# Revit family: PRD_FrankeWS_UrnlFlshPps_FlushingPipe_ZAQUA057_ZAQUA058_ZAQUA059_ZAQUA060
name_source: partatom
category: Specialty Equipment
revit_build: Autodesk Revit 2018 (Build: 20190510_1515(x64)
units: mm (PartAtom-declared; Revit-internal decimal feet)

## family parameters
Always vertical = Yes
Cut with Voids When Loaded = No
OmniClass Number = 23.45.05.14.99
OmniClass Title = Other Sanitary Washing Plumbing Fixtures
Part Type = Normal
Room Calculation Point = No
Round Connector Dimension = Use Diameter
Shared = No
Work Plane-Based = No

## types (4) — shared parameters
AssetType = Fixed
BodyMaterial = PRD_AR_ChromatedBrass_HighPolished
Category = Pr_40_20_93_80, Urinal flush pipes
Color = Chrome
Description = Flushing pipe for PROTRONIC urinal flush valve for surface installation, length 200 mm, polished chromium-plated brass.
DurationUnit = year
Finish = Polished chrome
IfcExportAs = IfcPipeFittingType
IfcExportType = USERDEFINED
Manufacturer = KWC Group AG
ManufacturerName = KWC Group AG
ManufacturerURL = www.kwc.com
Material = Brass
NBSDescription = Urinal flush pipes
NBSReference = 45-35-70/356
NominalHeight = 200 mm  [stored 0.656168 ft]
PressureClass = 0.0 Pa
PressureRange = 0.0 Pa
ProductInformation = https://pim.kwc.com
Status = New
TemperatureRange = 0 °C
TypeOfFlushingPipe = Urinal pipe
URL = www.kwc.com
Uniclass2015Code = Pr_40_20_93_80
Uniclass2015Title = Urinal flush pipes
Uniclass2015Version = Products v1.17
Version = 1
WarrantyDurationUnit = year
zero-valued in all types: FittingLossFactor, NominalDepth, NominalWidth

## per-type parameters (varying)
| type | BIMObjectName | Crank | Features | GrossWeight | ModelNumber | Name | NetWeight | ProductCode | WithCrank | ZAQUA057 | ZAQUA058 | ZAQUA059 | ZAQUA060 |
| ZAQUA057 | PRD_AR_UrinalFlushPipes_FlushingPipe_ZAQUA057 |  | Straight, length 200 mm | 0.08 kg | 2000101459 | Flushing pipe ZAQUA057 | 0.08 kg |  | No | Yes | No | No | No |
| ZAQUA058 | PRD_AR_UrinalFlushPipes_FlushingPipe_ZAQUA058 | 20.00 mm | With crank 20 mm, length 200 mm | 0.16 kg | 2000101460 | Flushing pipe ZAQUA058 | 0.09 kg | 209.0000.031 | Yes | No | Yes | No | No |
| ZAQUA059 | PRD_AR_UrinalFlushPipes_FlushingPipe_ZAQUA059 | 30.00 mm | With crank 30 mm, length 200 mm | 0.16 kg | 2000101461 | Flushing pipe ZAQUA059 | 0.09 kg | 209.0638.156 | Yes | No | No | Yes | No |
| ZAQUA060 | PRD_AR_UrinalFlushPipes_FlushingPipe_ZAQUA060 | 40.00 mm | With crank 40 mm, length 200 mm | 0.08 kg | 2000101462 | Flushing pipe ZAQUA060 | 0.08 kg | 209.0000.042 | Yes | No | No | No | Yes |

note: column(s) folded — value = type name in every type: Model, ModelReference

note: [stored X ft] marks values corroborated as IEEE doubles in the binary element streams (Revit-internal decimal feet)

## geometry (parser evidence)
native form markers: Sweep x2
no freeform markers — native parametric forms only
